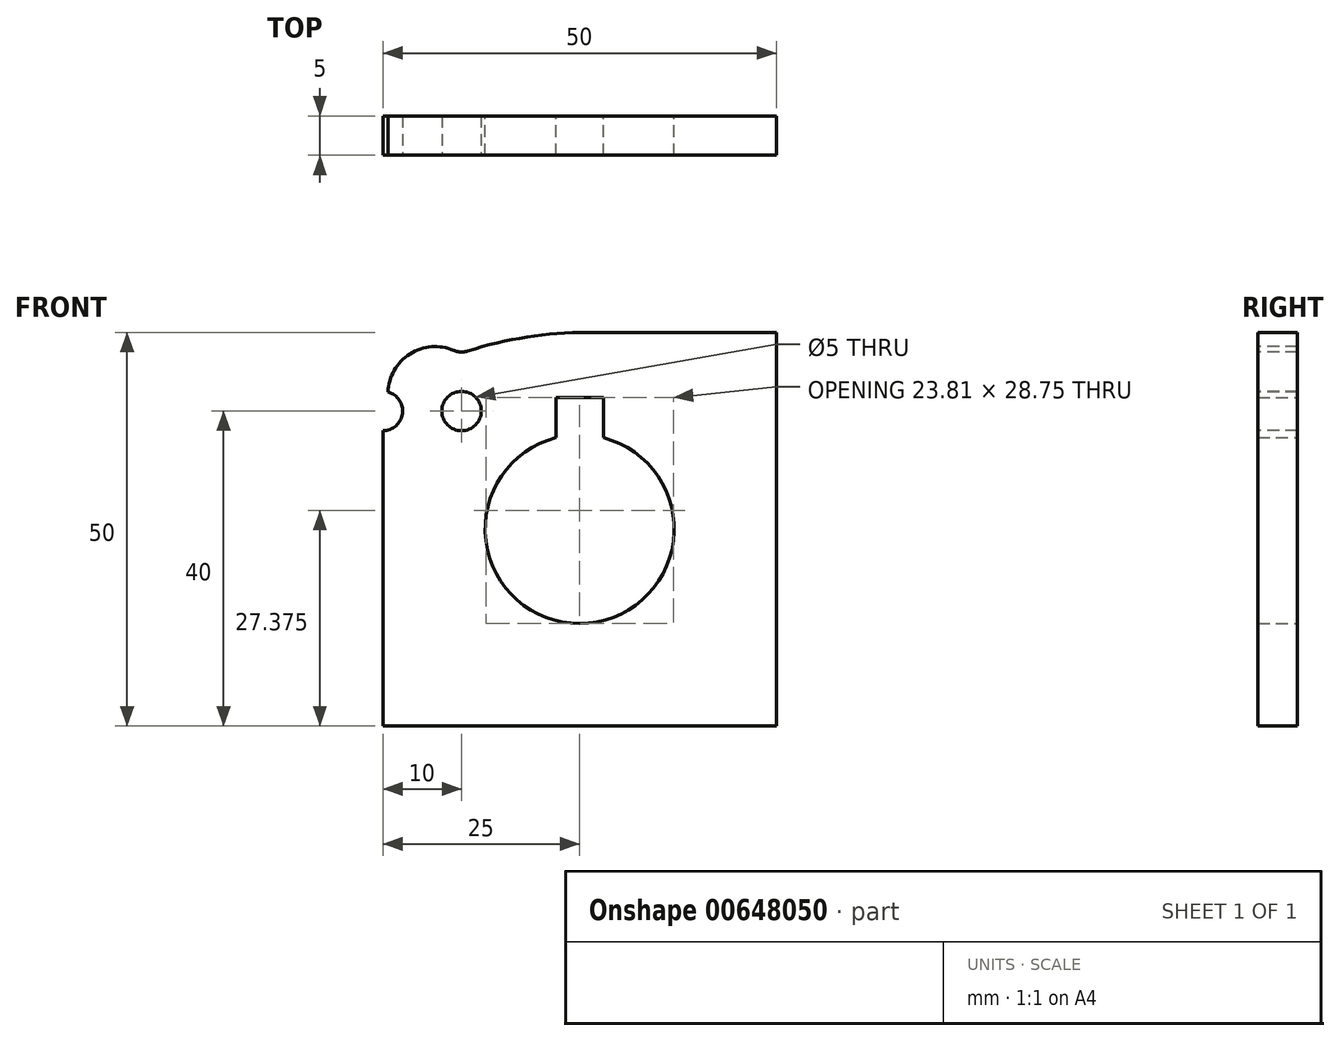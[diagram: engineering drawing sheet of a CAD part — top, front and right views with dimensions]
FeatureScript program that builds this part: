
annotation { "Feature Type Name" : "Feature", "Feature Type Description" : "" }
export const myFeature = defineFeature(function(context is Context, id is Id, definition is map)
    precondition{}
    {
        {
            var Q0;
            Q0=qCreatedBy(makeId("Front.planeOp"),FACE);
            var sketch = newSketch(context, id + "F0", { "sketchPlane" : qUnion([Q0])});
            skLineSegment(sketch, "E0.bottom", {"start": v(-25, 25) * mm, "end": v(25, 25) * mm});
            skLineSegment(sketch, "E0.top", {"start": v(-25, -25) * mm, "end": v(25, -25) * mm});
            skLineSegment(sketch, "E0.left", {"start": v(-25, 25) * mm, "end": v(-25, -25) * mm});
            skLineSegment(sketch, "E0.right", {"start": v(25, 25) * mm, "end": v(25, -25) * mm});
            skArc(sketch, "E1", {"start": v(-3, 11.62) * mm, "mid": v(0, -12) * mm, "end": v(3, 11.62) * mm});
            skLineSegment(sketch, "E2.bottom", {"start": v(-3, 16.75) * mm, "end": v(3, 16.75) * mm});
            skLineSegment(sketch, "E2.left", {"start": v(-3, 16.75) * mm, "end": v(-3, 11.62) * mm});
            skLineSegment(sketch, "E2.right", {"start": v(3, 16.75) * mm, "end": v(3, 11.62) * mm});
            skPoint(sketch, "E2.top.start.orphan", {"position": v(-3, 5.36) * mm});
            skSolve(sketch);
        }
        {
            var Q0;
            Q0 = qSketchRegion(id + "F0", true);
            extrude(context, id + "F1", {"entities" : qUnion([Q0]), "depth" : 5 * mm, "offsetDistance" : 25 * mm});
        }
        {
            var Q0;
            Q0=makeQuery(id+"F1.opExtrude","CAP_FACE",FACE,{"disambiguationData":[OSD([sQuery(id+"F0.wireOp",EDGE,"E0.bottom"),sQuery(id+"F0.wireOp",EDGE,"E0.top"),sQuery(id+"F0.wireOp",EDGE,"E0.left"),sQuery(id+"F0.wireOp",EDGE,"E0.right"),sQuery(id+"F0.wireOp",EDGE,"E1"),sQuery(id+"F0.wireOp",EDGE,"E2.bottom"),sQuery(id+"F0.wireOp",EDGE,"E2.left"),sQuery(id+"F0.wireOp",EDGE,"E2.right")])],"isStart":false});
            var sketch = newSketch(context, id + "F2", { "sketchPlane" : qUnion([Q0])});
            skCircle(sketch, "E3", {"center": v(-15, 15) * mm, "radius": 2.5 * mm});
            skArc(sketch, "E4", {"start": v(-25, 12.5) * mm, "mid": v(-22.52, 14.67) * mm, "end": v(-24.34, 17.41) * mm});
            skArc(sketch, "E5", {"start": v(-15.98, 22.7) * mm, "mid": v(-15.12, 22.5) * mm, "end": v(-14.24, 22.62) * mm});
            skArc(sketch, "E6", {"start": v(-9.94, 23.63) * mm, "mid": v(-10.04, 23.69) * mm, "end": v(-10.14, 23.74) * mm});
            skArc(sketch, "E7", {"start": v(-15.98, 22.7) * mm, "mid": v(-21.56, 22.26) * mm, "end": v(-24.34, 17.41) * mm});
            skArc(sketch, "E8.trimOffspring", {"start": v(1, 25) * mm, "mid": v(-6.7, 24.4) * mm, "end": v(-14.24, 22.62) * mm});
            skLineSegment(sketch, "E9.0", {"start": v(-25, 25) * mm, "end": v(25, 25) * mm});
            skLineSegment(sketch, "E10.0", {"start": v(-25, 25) * mm, "end": v(-25, -25) * mm});
            skSolve(sketch);
        }
        {
            var Q0;
            Q0 = qSketchRegion(id + "F2", true);
            extrude(context, id + "F3", {"entities" : qUnion([Q0]), "operationType" : NewBodyOperationType.REMOVE, "oppositeDirection" : true, "depth" : 25 * mm, "offsetDistance" : 25 * mm});
        }
    });
